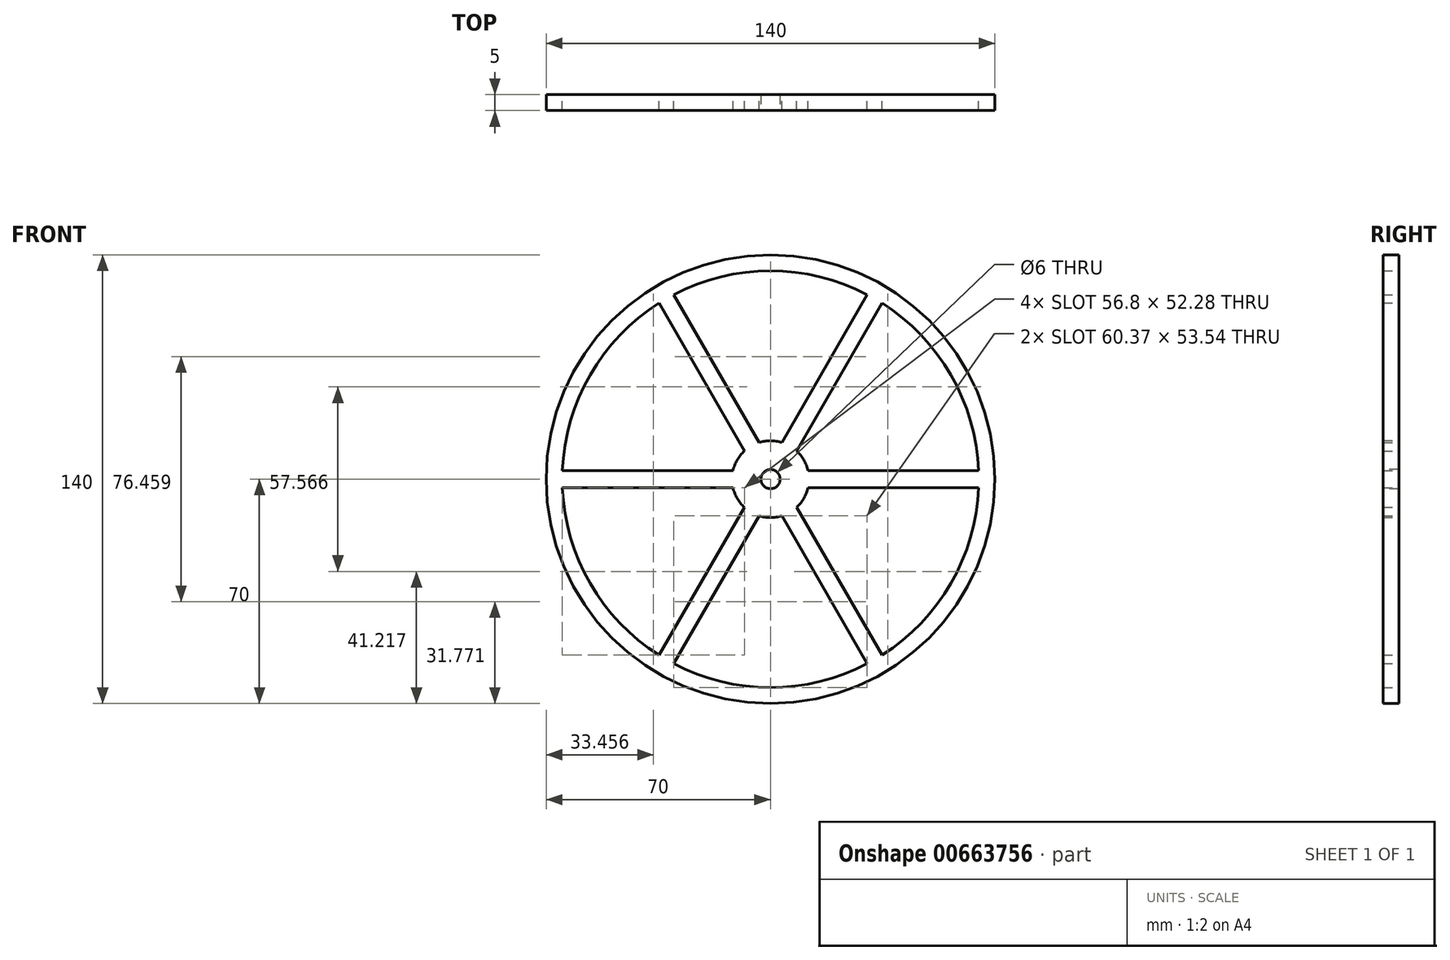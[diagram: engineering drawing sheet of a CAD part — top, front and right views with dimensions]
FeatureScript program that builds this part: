
annotation { "Feature Type Name" : "Feature", "Feature Type Description" : "" }
export const myFeature = defineFeature(function(context is Context, id is Id, definition is map)
    precondition{}
    {
        {
            var Q0;
            Q0=qCreatedBy(makeId("Front.planeOp"),FACE);
            var sketch = newSketch(context, id + "F0", { "sketchPlane" : qUnion([Q0])});
            skCircle(sketch, "E0", {"center": v(0, 0) * mm, "radius": 70 * mm});
            skSolve(sketch);
        }
        {
            var Q0;
            Q0 = qSketchRegion(id + "F0", true);
            extrude(context, id + "F1", {"entities" : qUnion([Q0]), "depth" : 5 * mm, "offsetDistance" : 25 * mm});
        }
        {
            var Q0;
            Q0=qCreatedBy(makeId("Front.planeOp"),FACE);
            var sketch = newSketch(context, id + "F2", { "sketchPlane" : qUnion([Q0])});
            skCircle(sketch, "E1", {"center": v(0, 0) * mm, "radius": 12 * mm});
            skCircle(sketch, "E2", {"center": v(0, 0) * mm, "radius": 65 * mm});
            skLineSegment(sketch, "E3.bottom", {"start": v(11.7, 2.64) * mm, "end": v(64.95, 2.64) * mm});
            skLineSegment(sketch, "E3.top", {"start": v(11.7, -2.64) * mm, "end": v(64.95, -2.64) * mm});
            skLineSegment(sketch, "E3.left", {"start": v(11.7, 2.64) * mm, "end": v(11.7, -2.64) * mm});
            skLineSegment(sketch, "E3.right", {"start": v(64.95, 2.64) * mm, "end": v(64.95, -2.64) * mm});
            skLineSegment(sketch, "E4", {"start": v(8.14, 8.82) * mm, "end": v(34.76, 54.92) * mm});
            skLineSegment(sketch, "E5", {"start": v(34.76, 54.92) * mm, "end": v(30.18, 57.57) * mm});
            skLineSegment(sketch, "E6", {"start": v(30.18, 57.57) * mm, "end": v(3.56, 11.46) * mm});
            skLineSegment(sketch, "E7", {"start": v(3.56, 11.46) * mm, "end": v(8.14, 8.82) * mm});
            skSolve(sketch);
        }
        {
            var Q0;
            {var subQ0=sQuery(id+"F2.wireOp",EDGE,"E3.bottom");Q0=makeQuery(id+"F2.imprint","IMPRINT",FACE,{"disambiguationData":[TD([[makeQuery(id+"F2.imprint","IMPRINT",EDGE,{"derivedFrom":subQ0}),1.0]])]});}
            extrude(context, id + "F3", {"entities" : qUnion([Q0]), "depth" : 25 * mm, "offsetDistance" : 25 * mm});
        }
        {
            var Q0;
            Q0=makeQuery(id+"F3.opExtrude","SWEPT_BODY",BODY,{"disambiguationData":[OSD([sQuery(id+"F2.wireOp",EDGE,"E1"),sQuery(id+"F2.wireOp",EDGE,"E2"),sQuery(id+"F2.wireOp",EDGE,"E3.bottom"),sQuery(id+"F2.wireOp",EDGE,"E4")])]});
            var Q1;
            Q1=makeQuery(id+"F3.opExtrude","SWEPT_FACE",FACE,{"disambiguationData":[OSD([sQuery(id+"F2.wireOp",EDGE,"E1")])]});
            circularPattern(context, id + "F4", {"operationType" : NewBodyOperationType.REMOVE, "entities" : qUnion([Q0]), "axis" : qUnion([Q1]), "angle" : 360 * degree, "instanceCount" : 6, "equalSpace" : true});
        }
        {
            var Q0;
            Q0=makeQuery(id+"F1.opExtrude","CAP_FACE",FACE,{"disambiguationData":[OSD([sQuery(id+"F0.wireOp",EDGE,"E0")])],"isStart":false});
            var sketch = newSketch(context, id + "F5", { "sketchPlane" : qUnion([Q0])});
            skCircle(sketch, "E8", {"center": v(0, 0) * mm, "radius": 3 * mm});
            skSolve(sketch);
        }
        {
            var Q0;
            Q0 = qSketchRegion(id + "F5", true);
            extrude(context, id + "F6", {"entities" : qUnion([Q0]), "operationType" : NewBodyOperationType.REMOVE, "endBound" : BoundingType.UP_TO_NEXT, "oppositeDirection" : true, "depth" : 25 * mm, "offsetDistance" : 25 * mm});
        }
    });
